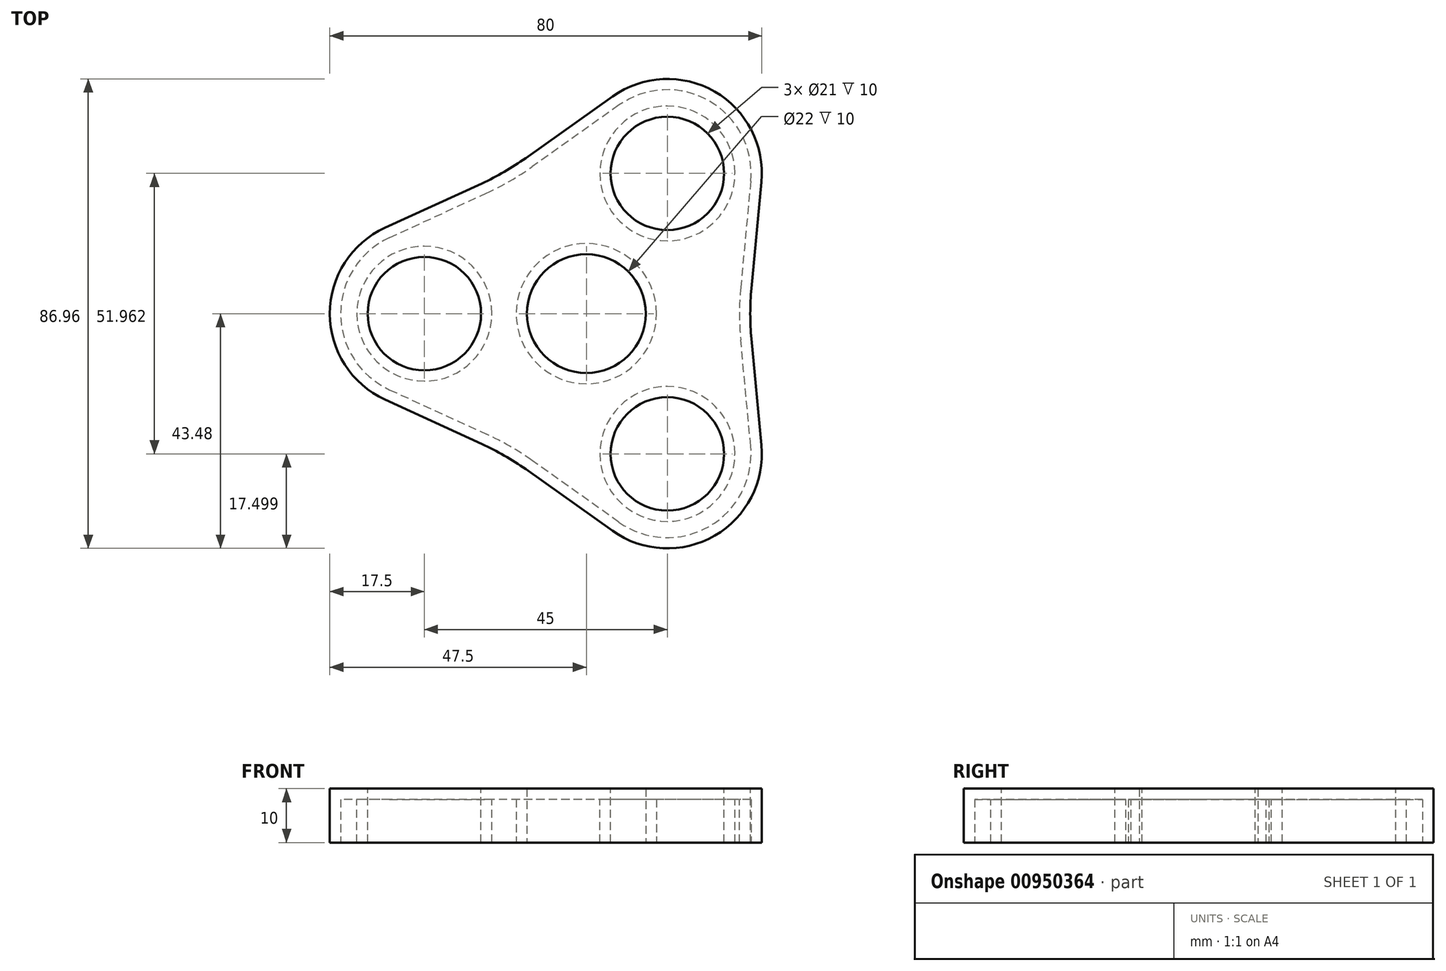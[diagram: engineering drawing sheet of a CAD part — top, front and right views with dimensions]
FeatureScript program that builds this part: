
annotation { "Feature Type Name" : "Feature", "Feature Type Description" : "" }
export const myFeature = defineFeature(function(context is Context, id is Id, definition is map)
    precondition{}
    {
        {
            var Q0;
            Q0=qCreatedBy(makeId("Top.planeOp"),FACE);
            var sketch = newSketch(context, id + "F0", { "sketchPlane" : qUnion([Q0])});
            skCircle(sketch, "E0", {"center": v(0, 0) * mm, "radius": 11 * mm});
            skLineSegment(sketch, "E1", {"start": v(0, 0) * mm, "end": v(-30, 0) * mm, "construction": true});
            skCircle(sketch, "E2", {"center": v(-30, 0) * mm, "radius": 11 * mm, "construction": true});
            skArc(sketch, "E3", {"start": v(-37.3, 15.9) * mm, "mid": v(-47.5, 0) * mm, "end": v(-37.3, -15.9) * mm});
            skLineSegment(sketch, "E4", {"start": v(-37.3, 15.9) * mm, "end": v(-12.5, 27.27) * mm});
            skLineSegment(sketch, "E5", {"start": v(-37.3, -15.9) * mm, "end": v(-12.5, -27.27) * mm});
            skArc(sketch, "E6.trimOffspring", {"start": v(-12.5, -27.27) * mm, "mid": v(30, 0) * mm, "end": v(-12.5, 27.27) * mm});
            skSolve(sketch);
        }
        {
            var Q0;
            Q0 = qSketchRegion(id + "F0", true);
            extrude(context, id + "F1", {"entities" : qUnion([Q0]), "depth" : 10 * mm, "offsetDistance" : 25 * mm});
        }
        {
            var Q0;
            Q0=makeQuery(id+"F1.opExtrude","SWEPT_BODY",BODY,{"disambiguationData":[OSD([sQuery(id+"F0.wireOp",EDGE,"E0"),sQuery(id+"F0.wireOp",EDGE,"E2"),sQuery(id+"F0.wireOp",EDGE,"E3"),sQuery(id+"F0.wireOp",EDGE,"E4"),sQuery(id+"F0.wireOp",EDGE,"E5"),sQuery(id+"F0.wireOp",EDGE,"E6.trimOffspring")])]});
            var Q1;
            Q1=makeQuery(id+"F1.opExtrude","SWEPT_FACE",FACE,{"disambiguationData":[OSD([sQuery(id+"F0.wireOp",EDGE,"E0")])]});
            circularPattern(context, id + "F2", {"entities" : qUnion([Q0]), "axis" : qUnion([Q1]), "angle" : 360 * degree, "instanceCount" : 3, "equalSpace" : true});
        }
        {
            var Q0;
            Q0=makeQuery(id+"F1.opExtrude","SWEPT_BODY",BODY,{"disambiguationData":[OSD([sQuery(id+"F0.wireOp",EDGE,"E0"),sQuery(id+"F0.wireOp",EDGE,"E3"),sQuery(id+"F0.wireOp",EDGE,"E4"),sQuery(id+"F0.wireOp",EDGE,"E5"),sQuery(id+"F0.wireOp",EDGE,"E6.trimOffspring")])]});
            var Q1;
            Q1=makeQuery(id+"F2.opPattern","COPY",BODY,{"derivedFrom":makeQuery(id+"F1.opExtrude","SWEPT_BODY",BODY,{"disambiguationData":[OSD([sQuery(id+"F0.wireOp",EDGE,"E0"),sQuery(id+"F0.wireOp",EDGE,"E3"),sQuery(id+"F0.wireOp",EDGE,"E4"),sQuery(id+"F0.wireOp",EDGE,"E5"),sQuery(id+"F0.wireOp",EDGE,"E6.trimOffspring")])]}),"instanceName":"1"});
            var Q2;
            Q2=makeQuery(id+"F2.opPattern","COPY",BODY,{"derivedFrom":makeQuery(id+"F1.opExtrude","SWEPT_BODY",BODY,{"disambiguationData":[OSD([sQuery(id+"F0.wireOp",EDGE,"E0"),sQuery(id+"F0.wireOp",EDGE,"E3"),sQuery(id+"F0.wireOp",EDGE,"E4"),sQuery(id+"F0.wireOp",EDGE,"E5"),sQuery(id+"F0.wireOp",EDGE,"E6.trimOffspring")])]}),"instanceName":"2"});
            booleanBodies(context, id + "F3", {"operationType" : BooleanOperationType.UNION, "tools" : qUnion([Q0, Q1, Q2])});
        }
        {
            var Q0;
            {var subQ0=makeQuery(id+"F1.opExtrude","CAP_FACE",FACE,{"disambiguationData":[OSD([sQuery(id+"F0.wireOp",EDGE,"E0"),sQuery(id+"F0.wireOp",EDGE,"E3"),sQuery(id+"F0.wireOp",EDGE,"E4"),sQuery(id+"F0.wireOp",EDGE,"E5"),sQuery(id+"F0.wireOp",EDGE,"E6.trimOffspring")])],"isStart":false});Q0=makeQuery(id+"F3.opBoolean","MERGE",FACE,{"derivedFrom":[subQ0,makeQuery(id+"F2.opPattern","COPY",FACE,{"derivedFrom":subQ0,"instanceName":"1"}),makeQuery(id+"F2.opPattern","COPY",FACE,{"derivedFrom":subQ0,"instanceName":"2"})]});}
            var sketch = newSketch(context, id + "F4", { "sketchPlane" : qUnion([Q0])});
            skCircle(sketch, "E7", {"center": v(15, 25.98) * mm, "radius": 10.5 * mm});
            skCircle(sketch, "E8", {"center": v(15, -25.98) * mm, "radius": 10.5 * mm});
            skCircle(sketch, "E9", {"center": v(-30, 0) * mm, "radius": 10.5 * mm});
            skSolve(sketch);
        }
        {
            var Q0;
            Q0=makeQuery(id+"F4.imprint","IMPRINT",FACE,{"disambiguationData":[TD([[makeQuery(id+"F4.imprint","IMPRINT",EDGE,{"derivedFrom":sQuery(id+"F4.wireOp",EDGE,"E7")}),1.0]])]});
            var Q1;
            Q1=makeQuery(id+"F4.imprint","IMPRINT",FACE,{"disambiguationData":[TD([[makeQuery(id+"F4.imprint","IMPRINT",EDGE,{"derivedFrom":sQuery(id+"F4.wireOp",EDGE,"E8")}),1.0]])]});
            var Q2;
            Q2=makeQuery(id+"F4.imprint","IMPRINT",FACE,{"disambiguationData":[TD([[makeQuery(id+"F4.imprint","IMPRINT",EDGE,{"derivedFrom":sQuery(id+"F4.wireOp",EDGE,"E9")}),1.0]])]});
            extrude(context, id + "F5", {"entities" : qUnion([Q0, Q1, Q2]), "operationType" : NewBodyOperationType.REMOVE, "oppositeDirection" : true, "depth" : 25 * mm, "offsetDistance" : 25 * mm});
        }
        {
            var Q0;
            Q0=makeQuery(id+"F3.opBoolean","INTERSECT",EDGE,{"derivedFrom":[makeQuery(id+"F2.opPattern","COPY",FACE,{"derivedFrom":makeQuery(id+"F1.opExtrude","SWEPT_FACE",FACE,{"disambiguationData":[OSD([sQuery(id+"F0.wireOp",EDGE,"E5")])]}),"instanceName":"1"}),makeQuery(id+"F2.opPattern","COPY",FACE,{"derivedFrom":makeQuery(id+"F1.opExtrude","SWEPT_FACE",FACE,{"disambiguationData":[OSD([sQuery(id+"F0.wireOp",EDGE,"E4")])]}),"instanceName":"2"})]});
            var Q1;
            Q1=makeQuery(id+"F3.opBoolean","INTERSECT",EDGE,{"derivedFrom":[makeQuery(id+"F1.opExtrude","SWEPT_FACE",FACE,{"disambiguationData":[OSD([sQuery(id+"F0.wireOp",EDGE,"E4")])]}),makeQuery(id+"F2.opPattern","COPY",FACE,{"derivedFrom":makeQuery(id+"F1.opExtrude","SWEPT_FACE",FACE,{"disambiguationData":[OSD([sQuery(id+"F0.wireOp",EDGE,"E5")])]}),"instanceName":"2"})]});
            var Q2;
            Q2=makeQuery(id+"F3.opBoolean","INTERSECT",EDGE,{"derivedFrom":[makeQuery(id+"F1.opExtrude","SWEPT_FACE",FACE,{"disambiguationData":[OSD([sQuery(id+"F0.wireOp",EDGE,"E5")])]}),makeQuery(id+"F2.opPattern","COPY",FACE,{"derivedFrom":makeQuery(id+"F1.opExtrude","SWEPT_FACE",FACE,{"disambiguationData":[OSD([sQuery(id+"F0.wireOp",EDGE,"E4")])]}),"instanceName":"1"})]});
            fillet(context, id + "F6", {"entities" : qUnion([Q0, Q1, Q2]), "radius" : 50 * mm, "tangentPropagation" : true, "allowEdgeOverflow" : false});
        }
        {
            var Q0;
            {var subQ0=makeQuery(id+"F1.opExtrude","CAP_FACE",FACE,{"disambiguationData":[OSD([sQuery(id+"F0.wireOp",EDGE,"E0"),sQuery(id+"F0.wireOp",EDGE,"E3"),sQuery(id+"F0.wireOp",EDGE,"E4"),sQuery(id+"F0.wireOp",EDGE,"E5"),sQuery(id+"F0.wireOp",EDGE,"E6.trimOffspring")])],"isStart":true});Q0=makeQuery(id+"F3.opBoolean","MERGE",FACE,{"derivedFrom":[subQ0,makeQuery(id+"F2.opPattern","COPY",FACE,{"derivedFrom":subQ0,"instanceName":"1"}),makeQuery(id+"F2.opPattern","COPY",FACE,{"derivedFrom":subQ0,"instanceName":"2"})]});}
            shell(context, id + "F7", {"entities" : qUnion([Q0]), "thickness" : 2 * mm});
        }
    });
